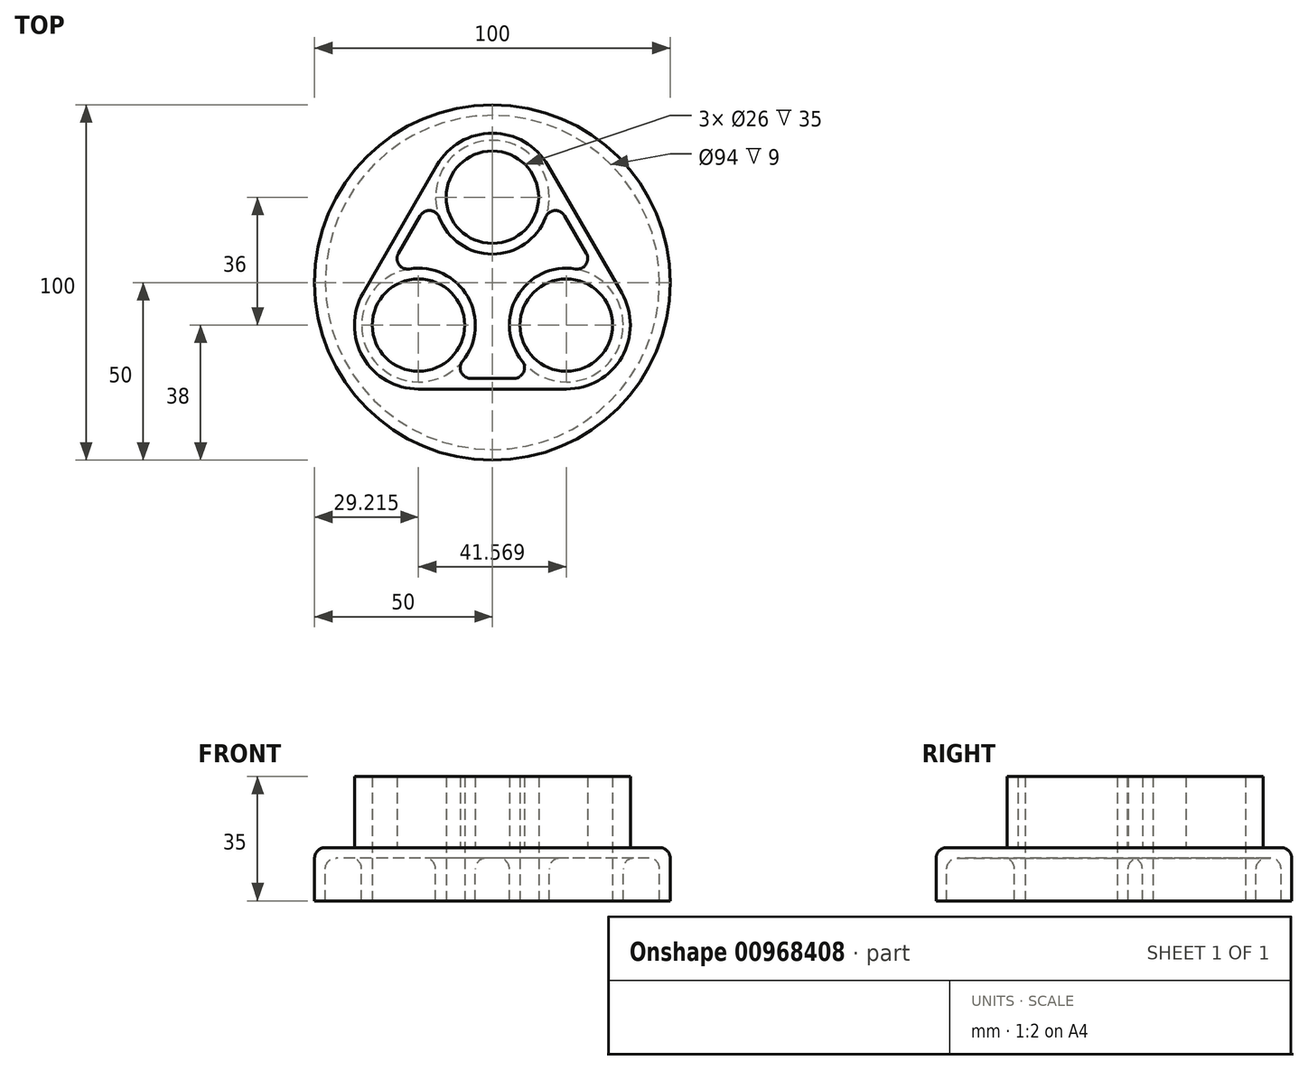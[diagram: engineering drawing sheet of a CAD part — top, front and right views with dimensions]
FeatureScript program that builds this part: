
annotation { "Feature Type Name" : "Feature", "Feature Type Description" : "" }
export const myFeature = defineFeature(function(context is Context, id is Id, definition is map)
    precondition{}
    {
        {
            var Q0;
            Q0=qCreatedBy(makeId("Top.planeOp"),FACE);
            var sketch = newSketch(context, id + "F0", { "sketchPlane" : qUnion([Q0])});
            skCircle(sketch, "E0", {"center": v(0, 0) * mm, "radius": 50 * mm, "construction": true});
            skCircle(sketch, "E1", {"center": v(0, 24) * mm, "radius": 13 * mm});
            skLineSegment(sketch, "E2", {"start": v(0, 0) * mm, "end": v(-20.78, -12) * mm, "construction": true});
            skLineSegment(sketch, "E3", {"start": v(0, 0) * mm, "end": v(20.78, -12) * mm, "construction": true});
            skCircle(sketch, "E4", {"center": v(-20.78, -12) * mm, "radius": 13 * mm});
            skCircle(sketch, "E5", {"center": v(20.78, -12) * mm, "radius": 13 * mm});
            skCircle(sketch, "E6", {"center": v(0, 0) * mm, "radius": 24 * mm, "construction": true});
            skArc(sketch, "E7", {"start": v(-15.59, 33) * mm, "mid": v(0, 42) * mm, "end": v(15.59, 33) * mm});
            skArc(sketch, "E8", {"start": v(-36.37, -3) * mm, "mid": v(-36.37, -21) * mm, "end": v(-20.78, -30) * mm});
            skArc(sketch, "E9", {"start": v(36.37, -3) * mm, "mid": v(36.37, -21) * mm, "end": v(20.78, -30) * mm});
            skLineSegment(sketch, "E10", {"start": v(-15.59, 33) * mm, "end": v(-36.37, -3) * mm});
            skLineSegment(sketch, "E11", {"start": v(15.59, 33) * mm, "end": v(36.37, -3) * mm});
            skLineSegment(sketch, "E12", {"start": v(-20.78, -30) * mm, "end": v(20.78, -30) * mm});
            skArc(sketch, "E13", {"start": v(-14.95, 18.3) * mm, "mid": v(0, 8) * mm, "end": v(14.95, 18.3) * mm});
            skArc(sketch, "E14", {"start": v(8.38, -22.1) * mm, "mid": v(6.93, -4) * mm, "end": v(23.33, 3.8) * mm});
            skArc(sketch, "E15", {"start": v(-23.33, 3.8) * mm, "mid": v(-6.93, -4) * mm, "end": v(-8.38, -22.1) * mm});
            skLineSegment(sketch, "E16", {"start": v(-6.05, -27) * mm, "end": v(6.05, -27) * mm});
            skLineSegment(sketch, "E17", {"start": v(20.36, 18.74) * mm, "end": v(26.4, 8.26) * mm});
            skLineSegment(sketch, "E18.0", {"start": v(-20.36, 18.74) * mm, "end": v(-26.4, 8.26) * mm});
            skPoint(sketch, "E19.visualSharp", {"position": v(-15.77, 26.68) * mm});
            skArc(sketch, "E19.filletArc", {"start": v(-14.95, 18.3) * mm, "mid": v(-17.52, 20.23) * mm, "end": v(-20.36, 18.74) * mm});
            skPoint(sketch, "E20.visualSharp", {"position": v(15.77, 26.68) * mm});
            skArc(sketch, "E20.filletArc", {"start": v(20.36, 18.74) * mm, "mid": v(17.52, 20.23) * mm, "end": v(14.95, 18.3) * mm});
            skPoint(sketch, "E21.visualSharp", {"position": v(31, 0.32) * mm});
            skArc(sketch, "E21.filletArc", {"start": v(23.33, 3.8) * mm, "mid": v(26.28, 5.05) * mm, "end": v(26.4, 8.26) * mm});
            skPoint(sketch, "E22.visualSharp", {"position": v(-31, 0.32) * mm});
            skArc(sketch, "E22.filletArc", {"start": v(-26.4, 8.26) * mm, "mid": v(-26.28, 5.05) * mm, "end": v(-23.33, 3.8) * mm});
            skPoint(sketch, "E23.visualSharp", {"position": v(15.22, -27) * mm});
            skArc(sketch, "E23.filletArc", {"start": v(6.05, -27) * mm, "mid": v(8.76, -25.29) * mm, "end": v(8.38, -22.1) * mm});
            skPoint(sketch, "E24.visualSharp", {"position": v(-15.22, -27) * mm});
            skArc(sketch, "E24.filletArc", {"start": v(-8.38, -22.1) * mm, "mid": v(-8.76, -25.29) * mm, "end": v(-6.05, -27) * mm});
            skSolve(sketch);
        }
        {
            var Q0;
            Q0=qCreatedBy(makeId("Top.planeOp"),FACE);
            var sketch = newSketch(context, id + "F1", { "sketchPlane" : qUnion([Q0])});
            skCircle(sketch, "E25.0", {"center": v(0, 0) * mm, "radius": 50 * mm});
            skCircle(sketch, "E26.0", {"center": v(0, 24) * mm, "radius": 13 * mm});
            skCircle(sketch, "E26.1", {"center": v(20.78, -12) * mm, "radius": 13 * mm});
            skCircle(sketch, "E26.2", {"center": v(-20.78, -12) * mm, "radius": 13 * mm});
            skCircle(sketch, "E27.0", {"center": v(0, 24) * mm, "radius": 16 * mm});
            skCircle(sketch, "E28.0", {"center": v(20.78, -12) * mm, "radius": 16 * mm});
            skCircle(sketch, "E29.0", {"center": v(-20.78, -12) * mm, "radius": 16 * mm});
            skSolve(sketch);
        }
        {
            var Q0;
            Q0 = qSketchRegion(id + "F1", true);
            var Q1;
            Q1=makeQuery(id+"F1.imprint","IMPRINT",FACE,{"disambiguationData":[TD([[makeQuery(id+"F1.imprint","IMPRINT",EDGE,{"derivedFrom":sQuery(id+"F1.wireOp",EDGE,"E26.2")}),-1.0]])]});
            var Q2;
            Q2=makeQuery(id+"F1.imprint","IMPRINT",FACE,{"disambiguationData":[TD([[makeQuery(id+"F1.imprint","IMPRINT",EDGE,{"derivedFrom":sQuery(id+"F1.wireOp",EDGE,"E26.2")}),1.0]])]});
            var Q3;
            Q3=makeQuery(id+"F1.imprint","IMPRINT",FACE,{"disambiguationData":[TD([[makeQuery(id+"F1.imprint","IMPRINT",EDGE,{"derivedFrom":sQuery(id+"F1.wireOp",EDGE,"E26.0")}),-1.0]])]});
            var Q4;
            Q4=makeQuery(id+"F1.imprint","IMPRINT",FACE,{"disambiguationData":[TD([[makeQuery(id+"F1.imprint","IMPRINT",EDGE,{"derivedFrom":sQuery(id+"F1.wireOp",EDGE,"E26.0")}),1.0]])]});
            var Q5;
            Q5=makeQuery(id+"F1.imprint","IMPRINT",FACE,{"disambiguationData":[TD([[makeQuery(id+"F1.imprint","IMPRINT",EDGE,{"derivedFrom":sQuery(id+"F1.wireOp",EDGE,"E26.1")}),-1.0]])]});
            var Q6;
            Q6=makeQuery(id+"F1.imprint","IMPRINT",FACE,{"disambiguationData":[TD([[makeQuery(id+"F1.imprint","IMPRINT",EDGE,{"derivedFrom":sQuery(id+"F1.wireOp",EDGE,"E26.1")}),1.0]])]});
            extrude(context, id + "F2", {"entities" : qUnion([Q0, Q1, Q2, Q3, Q4, Q5, Q6]), "oppositeDirection" : true, "depth" : 15 * mm, "offsetDistance" : 25 * mm});
        }
        {
            var Q0;
            Q0=makeQuery(id+"F2.opExtrude","CAP_FACE",FACE,{"disambiguationData":[OSD([sQuery(id+"F1.wireOp",EDGE,"E25.0")])],"isStart":false});
            shell(context, id + "F3", {"entities" : qUnion([Q0]), "thickness" : 3 * mm});
        }
        {
            var Q0;
            Q0=makeQuery(id+"F0.imprint","IMPRINT",FACE,{"disambiguationData":[TD([[makeQuery(id+"F0.imprint","IMPRINT",EDGE,{"derivedFrom":sQuery(id+"F0.wireOp",EDGE,"E1")}),-1.0]])]});
            extrude(context, id + "F4", {"entities" : qUnion([Q0]), "operationType" : NewBodyOperationType.ADD, "depth" : 20 * mm, "offsetDistance" : 25 * mm});
        }
        {
            var Q0;
            Q0=makeQuery(id+"F0.imprint","IMPRINT",FACE,{"disambiguationData":[TD([[makeQuery(id+"F0.imprint","IMPRINT",EDGE,{"derivedFrom":sQuery(id+"F0.wireOp",EDGE,"E1")}),1.0]])]});
            var Q1;
            Q1=makeQuery(id+"F0.imprint","IMPRINT",FACE,{"disambiguationData":[TD([[makeQuery(id+"F0.imprint","IMPRINT",EDGE,{"derivedFrom":sQuery(id+"F0.wireOp",EDGE,"E4")}),1.0]])]});
            var Q2;
            Q2=makeQuery(id+"F0.imprint","IMPRINT",FACE,{"disambiguationData":[TD([[makeQuery(id+"F0.imprint","IMPRINT",EDGE,{"derivedFrom":sQuery(id+"F0.wireOp",EDGE,"E5")}),1.0]])]});
            extrude(context, id + "F5", {"entities" : qUnion([Q0, Q1, Q2]), "operationType" : NewBodyOperationType.REMOVE, "endBound" : BoundingType.THROUGH_ALL, "oppositeDirection" : true, "depth" : 25 * mm, "offsetDistance" : 25 * mm});
        }
        {
            var Q0;
            Q0=makeQuery(id+"F1.imprint","IMPRINT",FACE,{"disambiguationData":[TD([[makeQuery(id+"F1.imprint","IMPRINT",EDGE,{"derivedFrom":sQuery(id+"F1.wireOp",EDGE,"E26.0")}),-1.0]])]});
            var Q1;
            Q1=makeQuery(id+"F1.imprint","IMPRINT",FACE,{"disambiguationData":[TD([[makeQuery(id+"F1.imprint","IMPRINT",EDGE,{"derivedFrom":sQuery(id+"F1.wireOp",EDGE,"E26.1")}),-1.0]])]});
            var Q2;
            Q2=makeQuery(id+"F1.imprint","IMPRINT",FACE,{"disambiguationData":[TD([[makeQuery(id+"F1.imprint","IMPRINT",EDGE,{"derivedFrom":sQuery(id+"F1.wireOp",EDGE,"E26.2")}),-1.0]])]});
            var Q3;
            Q3=makeQuery(id+"F2.opExtrude","CAP_FACE",FACE,{"disambiguationData":[OSD([sQuery(id+"F1.wireOp",EDGE,"E25.0")])],"isStart":false});
            extrude(context, id + "F6", {"entities" : qUnion([Q0, Q1, Q2]), "operationType" : NewBodyOperationType.ADD, "endBound" : BoundingType.UP_TO_SURFACE, "oppositeDirection" : true, "depth" : 25 * mm, "endBoundEntityFace" : qUnion([Q3]), "offsetDistance" : 25 * mm});
        }
        {
            var Q0;
            Q0=makeQuery(id+"F4.opExtrude","CAP_EDGE",EDGE,{"disambiguationData":[OSD([sQuery(id+"F0.wireOp",EDGE,"E17")])],"isStart":true});
            var Q1;
            Q1=makeQuery(id+"F4.opExtrude","CAP_EDGE",EDGE,{"disambiguationData":[OSD([sQuery(id+"F0.wireOp",EDGE,"E12")])],"isStart":true});
            var Q2;
            Q2=makeQuery(id+"F2.opExtrude","CAP_EDGE",EDGE,{"disambiguationData":[OSD([sQuery(id+"F1.wireOp",EDGE,"E25.0")])],"isStart":true});
            var Q3;
            {var subQ0=sQuery(id+"F1.wireOp",EDGE,"E25.0");Q3=makeQuery(id+"F3.opShell","OFFSET_EDGE",EDGE,{"disambiguationData":[OSD([subQ0]),TDD([makeQuery(id+"F2.opExtrude","CAP_EDGE",EDGE,{"disambiguationData":[OSD([subQ0])],"isStart":true})])]});}
            var Q4;
            {var subQ0=sQuery(id+"F1.wireOp",EDGE,"E25.0");Q4=makeQuery(id+"F6.boolean.opBoolean","INTERSECT",EDGE,{"derivedFrom":[makeQuery(id+"F3.opShell","OFFSET_FACE",FACE,{"disambiguationData":[OSD([subQ0]),TDD([makeQuery(id+"F2.opExtrude","CAP_FACE",FACE,{"disambiguationData":[OSD([subQ0])],"isStart":true})])]}),makeQuery(id+"F6.opExtrude","SWEPT_FACE",FACE,{"disambiguationData":[OSD([sQuery(id+"F1.wireOp",EDGE,"E29.0")])]})]});}
            var Q5;
            {var subQ0=sQuery(id+"F1.wireOp",EDGE,"E25.0");Q5=makeQuery(id+"F6.boolean.opBoolean","INTERSECT",EDGE,{"derivedFrom":[makeQuery(id+"F3.opShell","OFFSET_FACE",FACE,{"disambiguationData":[OSD([subQ0]),TDD([makeQuery(id+"F2.opExtrude","CAP_FACE",FACE,{"disambiguationData":[OSD([subQ0])],"isStart":true})])]}),makeQuery(id+"F6.opExtrude","SWEPT_FACE",FACE,{"disambiguationData":[OSD([sQuery(id+"F1.wireOp",EDGE,"E28.0")])]})]});}
            var Q6;
            {var subQ0=sQuery(id+"F1.wireOp",EDGE,"E25.0");Q6=makeQuery(id+"F6.boolean.opBoolean","INTERSECT",EDGE,{"derivedFrom":[makeQuery(id+"F3.opShell","OFFSET_FACE",FACE,{"disambiguationData":[OSD([subQ0]),TDD([makeQuery(id+"F2.opExtrude","CAP_FACE",FACE,{"disambiguationData":[OSD([subQ0])],"isStart":true})])]}),makeQuery(id+"F6.opExtrude","SWEPT_FACE",FACE,{"disambiguationData":[OSD([sQuery(id+"F1.wireOp",EDGE,"E27.0")])]})]});}
            fillet(context, id + "F7", {"entities" : qUnion([Q0, Q1, Q2, Q3, Q4, Q5, Q6]), "tangentPropagation" : true, "radius" : 3 * mm, "defaultsChanged" : false, "vertexSettings" : [], "allowEdgeOverflow" : false});
        }
    });
